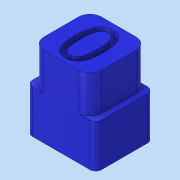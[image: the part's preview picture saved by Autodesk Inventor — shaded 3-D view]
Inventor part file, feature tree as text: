
AUTODESK INVENTOR PART (.ipt)
format: ipt  version: 2018 (Build 220112000, 112)  size: 177,152 bytes
history: native  units: mm
features: sketch x3, extrude x2, fillet x2, other x1, projected_geometry x1
ambient origin geometry x8: Origin, YZ Plane, XZ Plane, XY Plane, X Axis, Y Axis, Z Axis, Center Point
bodies: Volumenkörper1 (feature_tree)
feature tree (9):
  extrude  "Extrusion1"  Depth=10.0mm
  extrude  "Extrusion2"  Depth=10.0mm
  fillet  "Rundung1"  Radius=10.0mm
  fillet  "Rundung2"  Radius=6.5mm
  other  "Prägen1"
  sketch  "Skizze1"  dims[d0=12.0mm d1=10.0mm]
  sketch  "Skizze2"  dims[d2=14.0mm d3=0.0mm d4=10.0mm d5=10.0mm d6=6.5mm d7=0.0mm]
  sketch  "Skizze3"  dims[d8=2.0mm d9=1.0mm d10=1.0mm d11=1.0mm d12=1.0mm d13=3.490659mm]
  projected_geometry  "Projizierte Kontur1"
